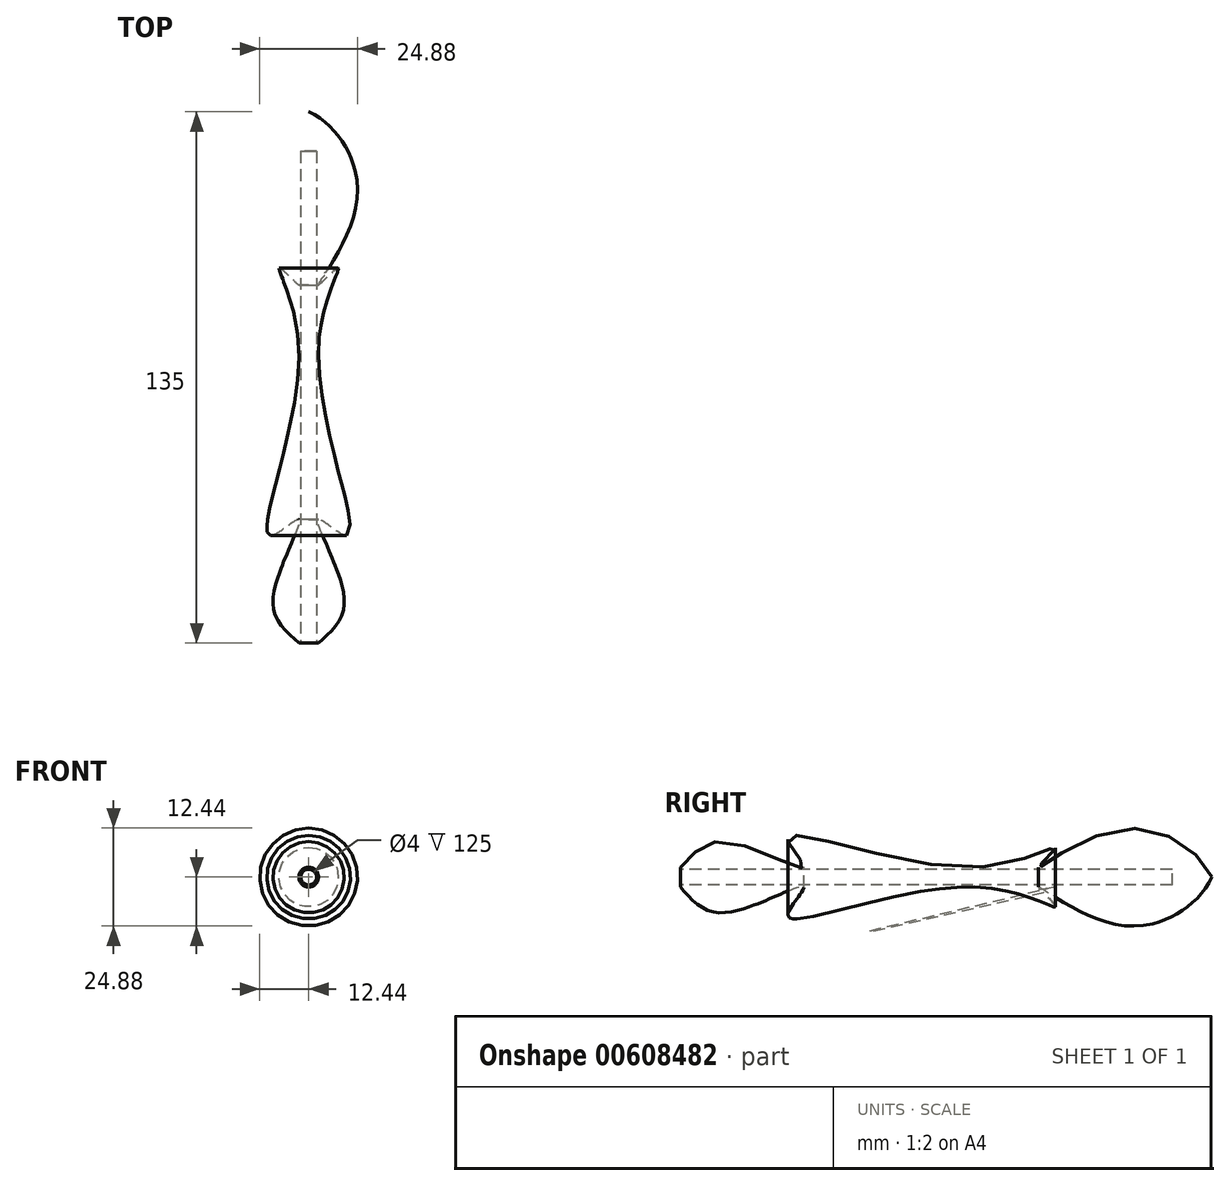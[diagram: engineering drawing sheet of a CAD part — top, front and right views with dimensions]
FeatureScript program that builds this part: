
annotation { "Feature Type Name" : "Feature", "Feature Type Description" : "" }
export const myFeature = defineFeature(function(context is Context, id is Id, definition is map)
    precondition{}
    {
        {
            var Q0;
            Q0=qCreatedBy(makeId("Right.planeOp"),FACE);
            var sketch = newSketch(context, id + "F0", { "sketchPlane" : qUnion([Q0])});
            skLineSegment(sketch, "E0", {"start": v(0, 0) * mm, "end": v(135, 0) * mm});
            skLineSegment(sketch, "E1", {"start": v(0, 0) * mm, "end": v(0, 2.5) * mm});
            skFitSpline(sketch, "E2", {"points": [v(0, 2.5) * mm, v(11.4, 9.02) * mm, v(31.46, 2.5) * mm, v(27.36, 9.75) * mm, v(74.92, 2.5) * mm, v(95.26, 7.25) * mm, v(91.02, 2.5) * mm, v(112.24, 12.26) * mm, v(135, 0) * mm], "startDerivative": vector(85.7, 90.86) * mm, "endDerivative": vector(53.16, -130.44) * mm});
            skSolve(sketch);
        }
        {
            var Q0;
            Q0=makeQuery(id+"F0.imprint","IMPRINT",FACE,{"disambiguationData":[TD([[makeQuery(id+"F0.imprint","IMPRINT",EDGE,{"derivedFrom":sQuery(id+"F0.wireOp",EDGE,"E0")}),1.0]])]});
            var Q1;
            Q1=sQuery(id+"F0.wireOp",EDGE,"E0");
            revolve(context, id + "F1", {"entities" : qUnion([Q0]), "axis" : qUnion([Q1]), "revolveType" : RevolveType.FULL});
        }
        {
            var Q0;
            Q0=makeQuery(id+"F1.opRevolve","SWEPT_FACE",FACE,{"disambiguationData":[OSD([sQuery(id+"F0.wireOp",EDGE,"E1")])]});
            var sketch = newSketch(context, id + "F2", { "sketchPlane" : qUnion([Q0])});
            skCircle(sketch, "E3", {"center": v(0, 0) * mm, "radius": 2 * mm});
            skSolve(sketch);
        }
        {
            var Q0;
            Q0=makeQuery(id+"F2.imprint","IMPRINT",FACE,{"disambiguationData":[TD([[makeQuery(id+"F2.imprint","IMPRINT",EDGE,{"derivedFrom":sQuery(id+"F2.wireOp",EDGE,"E3")}),1.0]])]});
            extrude(context, id + "F3", {"entities" : qUnion([Q0]), "operationType" : NewBodyOperationType.REMOVE, "oppositeDirection" : true, "depth" : 125 * mm, "offsetDistance" : 25 * mm});
        }
    });
